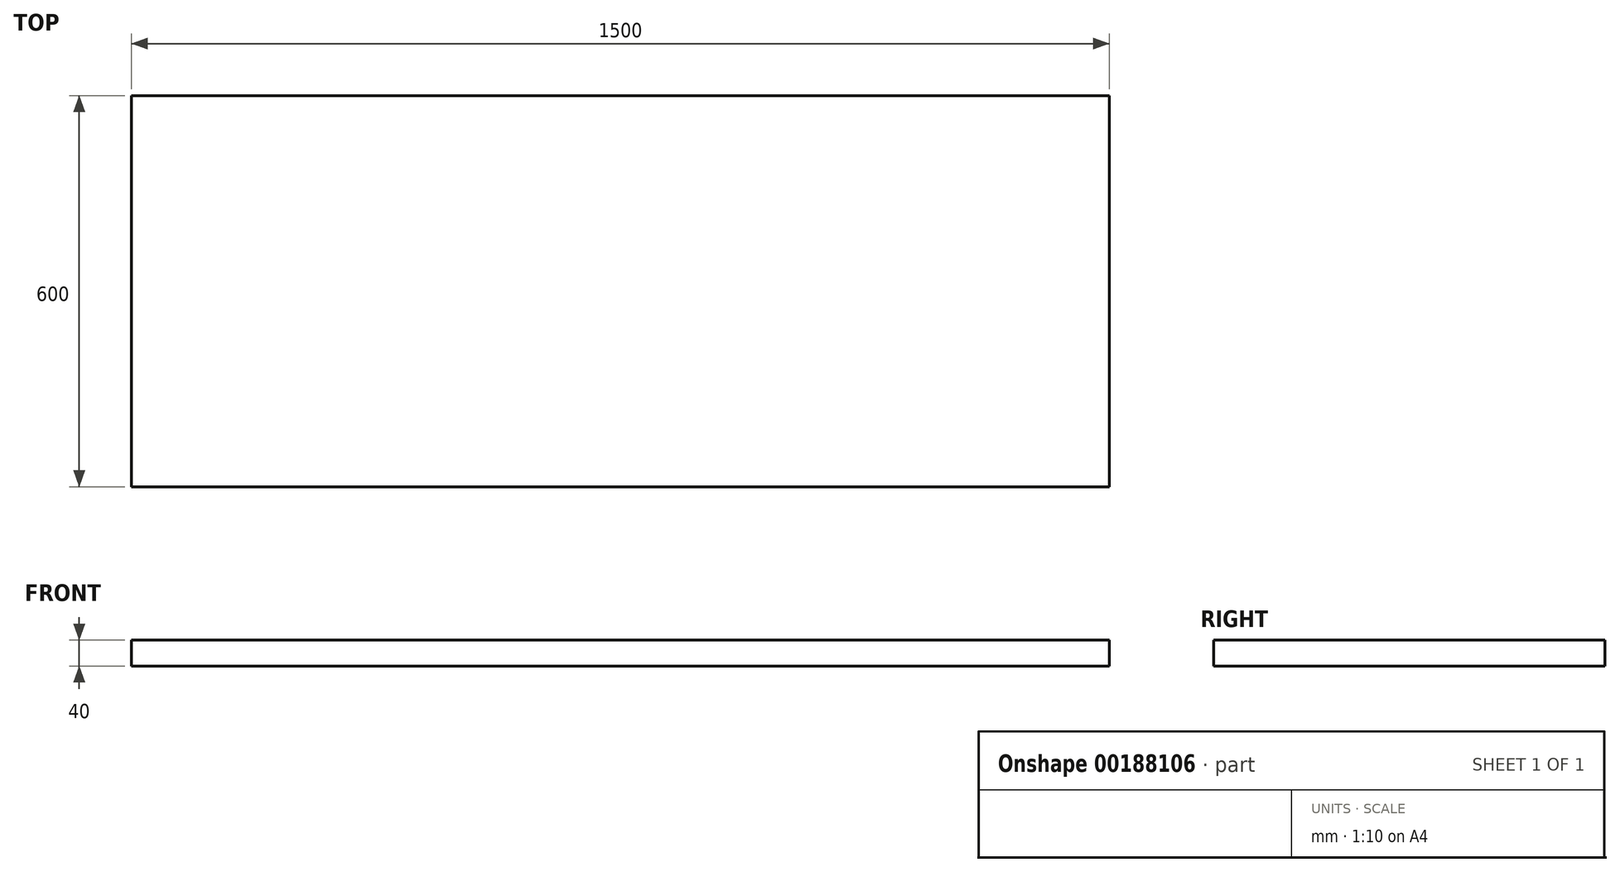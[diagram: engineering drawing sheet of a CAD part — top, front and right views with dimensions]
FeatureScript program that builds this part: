
annotation { "Feature Type Name" : "Feature", "Feature Type Description" : "" }
export const myFeature = defineFeature(function(context is Context, id is Id, definition is map)
    precondition{}
    {
        {
            var Q0;
            Q0=qCreatedBy(makeId("Top.planeOp"),FACE);
            var sketch = newSketch(context, id + "F0", { "sketchPlane" : qUnion([Q0])});
            skLineSegment(sketch, "E0.bottom", {"start": v(-467.38, -254.02) * mm, "end": v(1032.62, -254.02) * mm});
            skLineSegment(sketch, "E0.top", {"start": v(-467.38, 345.98) * mm, "end": v(1032.62, 345.98) * mm});
            skLineSegment(sketch, "E0.left", {"start": v(-467.38, -254.02) * mm, "end": v(-467.38, 345.98) * mm});
            skLineSegment(sketch, "E0.right", {"start": v(1032.62, -254.02) * mm, "end": v(1032.62, 345.98) * mm});
            skSolve(sketch);
        }
        {
            var Q0;
            Q0=makeQuery(id+"F0.imprint","IMPRINT",FACE,{"disambiguationData":[TD([[makeQuery(id+"F0.imprint","IMPRINT",EDGE,{"derivedFrom":sQuery(id+"F0.wireOp",EDGE,"E0.bottom")}),1.0]])]});
            extrude(context, id + "F1", {"entities" : qUnion([Q0]), "depth" : 40 * mm});
        }
    });
